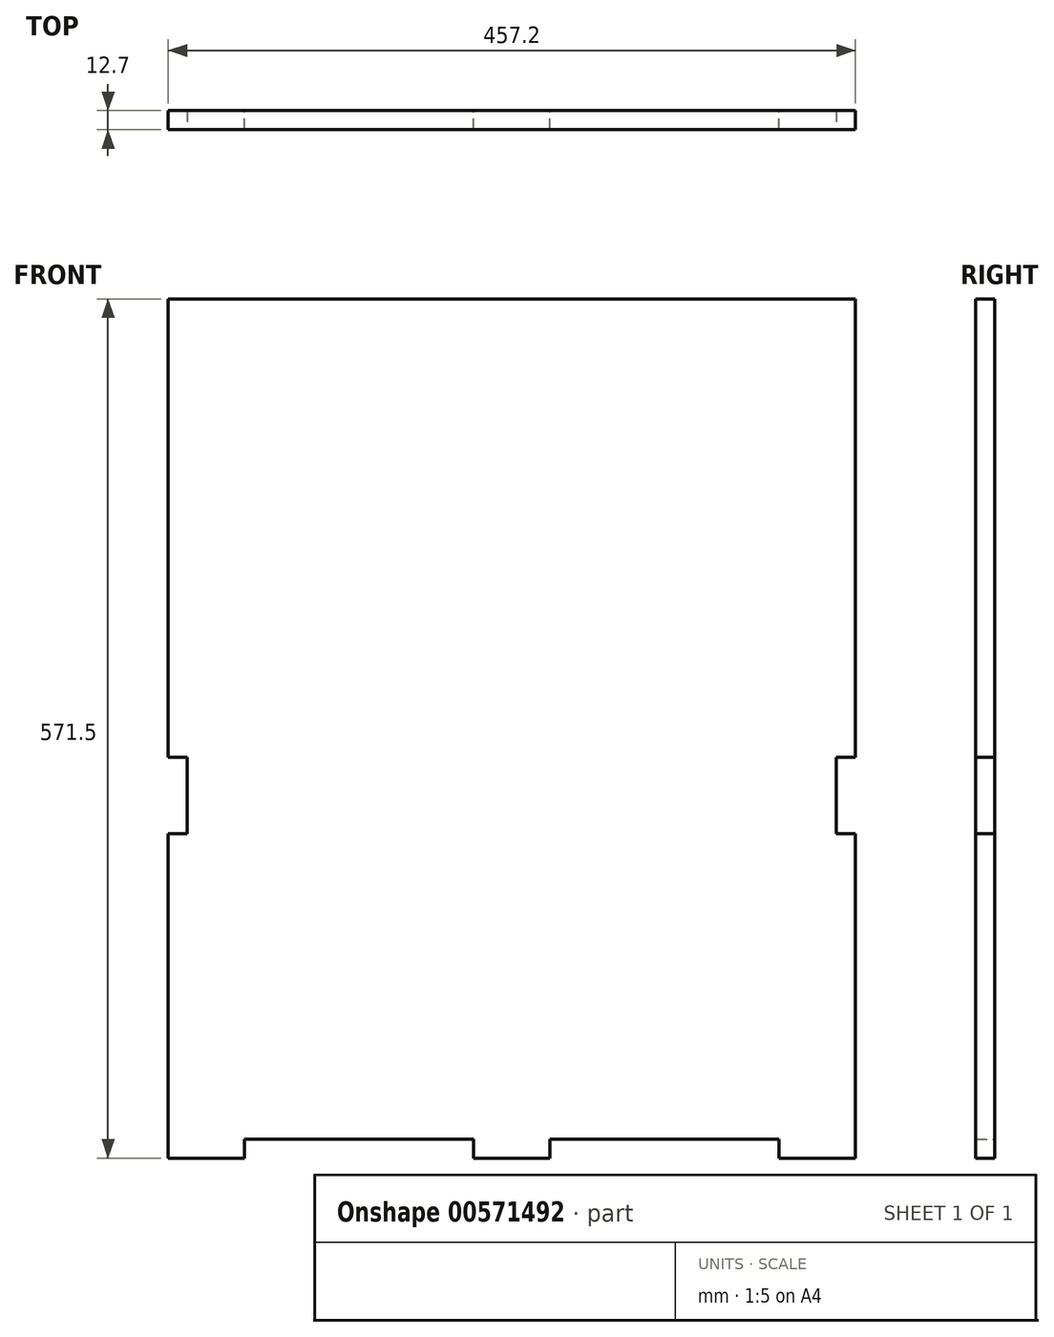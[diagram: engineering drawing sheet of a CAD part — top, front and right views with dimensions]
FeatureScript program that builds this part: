
annotation { "Feature Type Name" : "Feature", "Feature Type Description" : "" }
export const myFeature = defineFeature(function(context is Context, id is Id, definition is map)
    precondition{}
    {
        {
            var Q0;
            Q0=qCreatedBy(makeId("Front.planeOp"),FACE);
            var sketch = newSketch(context, id + "F0", { "sketchPlane" : qUnion([Q0])});
            skLineSegment(sketch, "E0.bottom", {"start": v(177.8, -273.29) * mm, "end": v(25.4, -273.29) * mm});
            skLineSegment(sketch, "E0.top", {"start": v(228.6, 285.51) * mm, "end": v(-228.6, 285.51) * mm});
            skLineSegment(sketch, "E0.left", {"start": v(228.6, -273.29) * mm, "end": v(228.6, 285.51) * mm});
            skLineSegment(sketch, "E0.right", {"start": v(-228.6, -273.29) * mm, "end": v(-228.6, 285.51) * mm});
            skPoint(sketch, "E0.middle", {"position": v(0, 6.11) * mm});
            skLineSegment(sketch, "E1.top", {"start": v(-228.6, -285.99) * mm, "end": v(-177.8, -285.99) * mm});
            skLineSegment(sketch, "E1.left", {"start": v(-228.6, -273.29) * mm, "end": v(-228.6, -285.99) * mm});
            skLineSegment(sketch, "E1.right", {"start": v(-177.8, -273.29) * mm, "end": v(-177.8, -285.99) * mm});
            skLineSegment(sketch, "E2.top", {"start": v(228.6, -285.99) * mm, "end": v(177.8, -285.99) * mm});
            skLineSegment(sketch, "E2.left", {"start": v(228.6, -273.29) * mm, "end": v(228.6, -285.99) * mm});
            skLineSegment(sketch, "E2.right", {"start": v(177.8, -273.29) * mm, "end": v(177.8, -285.99) * mm});
            skLineSegment(sketch, "E3.bottom", {"start": v(25.4, -285.99) * mm, "end": v(-25.4, -285.99) * mm});
            skLineSegment(sketch, "E3.left", {"start": v(25.4, -285.99) * mm, "end": v(25.4, -273.29) * mm});
            skLineSegment(sketch, "E3.right", {"start": v(-25.4, -285.99) * mm, "end": v(-25.4, -273.29) * mm});
            skPoint(sketch, "E3.middle", {"position": v(0, -273.29) * mm});
            skPoint(sketch, "E3.top.end.orphan", {"position": v(-25.4, -260.59) * mm});
            skPoint(sketch, "E4.orphan", {"position": v(25.4, -260.59) * mm});
            skLineSegment(sketch, "E5.trimOffspring", {"start": v(-25.4, -273.29) * mm, "end": v(-177.8, -273.29) * mm});
            skLineSegment(sketch, "E6", {"start": v(-228.6, -273.29) * mm, "end": v(-228.6, -85.56) * mm, "construction": true});
            skSolve(sketch);
        }
        {
            var Q0;
            Q0 = qSketchRegion(id + "F0", true);
            extrude(context, id + "F1", {"entities" : qUnion([Q0]), "depth" : 12.7 * mm, "offsetDistance" : 25.4 * mm});
        }
        {
            var Q0;
            Q0=makeQuery(id+"F1.opExtrude","CAP_FACE",FACE,{"disambiguationData":[OSD([sQuery(id+"F0.wireOp",EDGE,"E0.bottom"),sQuery(id+"F0.wireOp",EDGE,"E0.top"),sQuery(id+"F0.wireOp",EDGE,"E0.left"),sQuery(id+"F0.wireOp",EDGE,"E0.right"),sQuery(id+"F0.wireOp",EDGE,"E1.top"),sQuery(id+"F0.wireOp",EDGE,"E1.left"),sQuery(id+"F0.wireOp",EDGE,"E1.right"),sQuery(id+"F0.wireOp",EDGE,"E2.top"),sQuery(id+"F0.wireOp",EDGE,"E2.left"),sQuery(id+"F0.wireOp",EDGE,"E2.right"),sQuery(id+"F0.wireOp",EDGE,"E3.bottom"),sQuery(id+"F0.wireOp",EDGE,"E3.left"),sQuery(id+"F0.wireOp",EDGE,"E3.right"),sQuery(id+"F0.wireOp",EDGE,"E5.trimOffspring")])],"isStart":false});
            var sketch = newSketch(context, id + "F2", { "sketchPlane" : qUnion([Q0])});
            skLineSegment(sketch, "E7", {"start": v(-228.6, -273.29) * mm, "end": v(-228.6, -70.09) * mm, "construction": true});
            skLineSegment(sketch, "E8.bottom", {"start": v(-228.6, -70.09) * mm, "end": v(-215.9, -70.09) * mm});
            skLineSegment(sketch, "E8.top", {"start": v(-228.6, -19.29) * mm, "end": v(-215.9, -19.29) * mm});
            skLineSegment(sketch, "E8.left", {"start": v(-228.6, -70.09) * mm, "end": v(-228.6, -19.29) * mm});
            skLineSegment(sketch, "E8.right", {"start": v(-215.9, -70.09) * mm, "end": v(-215.9, -19.29) * mm});
            skLineSegment(sketch, "E9", {"start": v(-215.9, -70.09) * mm, "end": v(228.6, -70.09) * mm, "construction": true});
            skLineSegment(sketch, "E10.bottom", {"start": v(228.6, -70.09) * mm, "end": v(215.9, -70.09) * mm});
            skLineSegment(sketch, "E10.top", {"start": v(228.6, -19.29) * mm, "end": v(215.9, -19.29) * mm});
            skLineSegment(sketch, "E10.left", {"start": v(228.6, -70.09) * mm, "end": v(228.6, -19.29) * mm});
            skLineSegment(sketch, "E10.right", {"start": v(215.9, -70.09) * mm, "end": v(215.9, -19.29) * mm});
            skSolve(sketch);
        }
        {
            var Q0;
            Q0 = qSketchRegion(id + "F2", true);
            extrude(context, id + "F3", {"entities" : qUnion([Q0]), "operationType" : NewBodyOperationType.REMOVE, "oppositeDirection" : true, "depth" : 25.4 * mm, "offsetDistance" : 25.4 * mm});
        }
    });
